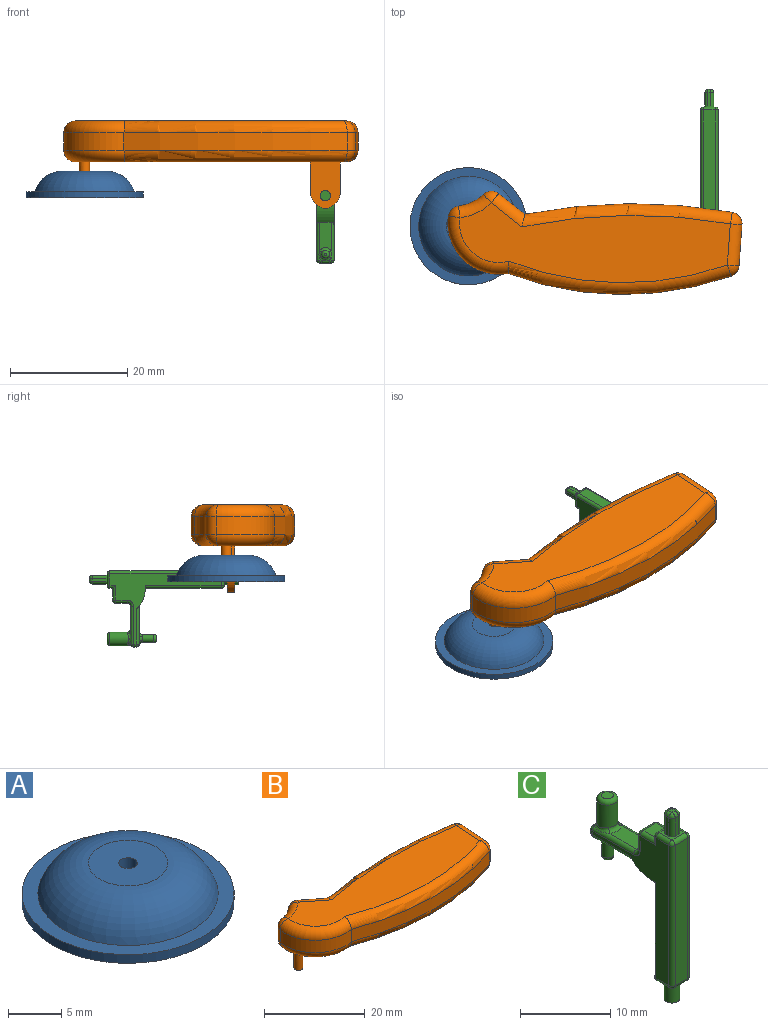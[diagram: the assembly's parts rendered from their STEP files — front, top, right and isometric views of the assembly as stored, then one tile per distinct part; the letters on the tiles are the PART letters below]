
ASSEMBLY  parts=3 mates=2
PART A: 8 faces, bbox 20x20x5 mm
  f0: cylinder r=10mm len=20mm, axis (0,0,-1), area 62.8mm2, adj f1,f2
  f1: plane 20x20mm, normal (0,0,1), area 87.2mm2, adj f0,f4
  f2: plane 20x20mm, normal (0,0,-1), area 194.2mm2, adj f0,f5
  f3: plane 7.46x7.46mm, normal (0,0,1), area 41.3mm2, adj f4,f7
  f4: torus R=3.73mm, axis (0,0,-1), area 258.3mm2, adj f1,f3
  f5: torus R=3.73mm, axis (0,0,-1), area 111.7mm2, adj f2,f6
  f6: plane 7.46x7.46mm, normal (0,0,-1), area 41.3mm2, adj f5,f7
  f7: cylinder r=0.88mm len=2.5mm, axis (0,0,1), area 13.7mm2, adj f3,f6
PART B: 47 faces, bbox 50.9x22.2x15 mm
  f0: cylinder r=96.06mm len=35.42mm, axis (0,0,-1), area 106.9mm2, adj f1,f15,f21,f24
  f1: plane 4.48x3.53mm, normal (0.62,0.78,0), area 17.1mm2, adj f0,f25,f28,f31
  f2: cylinder r=7.26mm len=4.21mm, axis (0,0,-1), area 14.2mm2, adj f18,f26,f27,f31
  f3: cylinder r=8.71mm len=10.27mm, axis (0,0,-1), area 49.4mm2, adj f4,f17,f18,f19
  f4: cylinder r=55.62mm len=38.1mm, axis (0,0,-1), area 116.7mm2, adj f3,f8,f12,f13
  f5: plane 7.03x3mm, normal (1,-0.07,0), area 21.1mm2, adj f8,f11,f14,f15
  f6: plane 46.22x13.65mm, normal (0,0,1), area 431.2mm2, adj f11,f12,f17,f21,f25,f26
  f7: plane 46.22x13.65mm, normal (0,0,-1), area 155mm2, adj f13,f14,f19,f24,f27,f28,f32,f33
  f8: cylinder r=2mm len=3mm, axis (0,0,-1), area 7mm2, adj f4,f5,f9,f10
  f9: sphere r=2mm, area 4.6mm2, adj f8,f11,f12
  f10: sphere r=2mm, area 4.6mm2, adj f8,f13,f14
  f11: cylinder r=2mm len=7.17mm, axis (-0.07,-1,0), area 22.1mm2, adj f5,f6,f9,f16
  f12: torus R=53.62mm, axis (0,0,1), area 121.2mm2, adj f4,f6,f9,f17
  f13: torus R=53.62mm, axis (0,0,1), area 121.2mm2, adj f4,f7,f10,f19
  f14: cylinder r=2mm len=7.17mm, axis (0.07,1,0), area 22.1mm2, adj f5,f7,f10,f20
  f15: cylinder r=2mm len=3mm, axis (0,0,-1), area 8.8mm2, adj f0,f5,f16,f20
  f16: sphere r=2mm, area 5.9mm2, adj f11,f15,f21
  f17: torus R=6.71mm, axis (0,0,1), area 48.1mm2, adj f3,f6,f12,f22
  f18: cylinder r=2mm len=3mm, axis (0,0,1), area 7.9mm2, adj f2,f3,f22,f23
  f19: torus R=6.71mm, axis (0,0,1), area 48.1mm2, adj f3,f7,f13,f23
  f20: sphere r=2mm, area 5.9mm2, adj f14,f15,f24
  f21: torus R=94.06mm, axis (0,0,1), area 112.1mm2, adj f0,f6,f16,f25
  f22: sphere r=2mm, area 5.3mm2, adj f17,f18,f26
  f23: sphere r=2mm, area 5.3mm2, adj f18,f19,f27
  f24: torus R=94.06mm, axis (0,0,1), area 112.1mm2, adj f0,f7,f20,f28
  f25: cylinder r=2mm len=6.44mm, axis (0.78,-0.62,0), area 19mm2, adj f1,f6,f21,f29
  f26: torus R=9.26mm, axis (0,0,1), area 16.4mm2, adj f2,f6,f22,f29
  f27: torus R=9.26mm, axis (0,0,1), area 16.4mm2, adj f2,f7,f23,f30
  f28: cylinder r=2mm len=6.44mm, axis (-0.78,0.62,0), area 19mm2, adj f1,f7,f24,f30
  f29: sphere r=2mm, area 5.8mm2, adj f25,f26,f31
  f30: sphere r=2mm, area 5.8mm2, adj f27,f28,f31
  f31: cylinder r=2mm len=3mm, axis (0,0,-1), area 8.6mm2, adj f1,f2,f29,f30
  f32: cylinder r=8.82mm len=7.3mm, axis (0,0,-1), area 24.1mm2, adj f7,f33,f36,f37
  f33: cylinder r=34.45mm len=30.65mm, axis (0,0,-1), area 95.5mm2, adj f7,f32,f34,f37
  f34: cylinder r=0.98mm len=3mm, axis (0,0,-1), area 6.5mm2, adj f7,f33,f35,f37
  f35: cylinder r=40.15mm len=36.75mm, axis (0,0,-1), area 114.7mm2, adj f7,f34,f36,f37
  f36: cylinder r=2.07mm len=4.13mm, axis (0,0,-1), area 23.4mm2, adj f7,f32,f35,f37
  f37: plane 40.56x9.64mm, normal (0,0,-1), area 267.3mm2, adj f32,f33,f34,f35,f36
  f38: cylinder r=0.88mm len=5mm, axis (0,0,1), area 27.5mm2, adj f7,f39
  f39: plane 1.75x1.75mm, normal (0,0,-1), area 2.4mm2, adj f38
  f40: plane 5x1.27mm, normal (-1,0,0), area 6.3mm2, adj f7,f41,f43,f44
  f41: plane 7.97x5.13mm, normal (0,1,0), area 34.8mm2, adj f7,f40,f42,f44,f45,f46
  f42: plane 5x1.27mm, normal (1,0,0), area 6.3mm2, adj f7,f41,f43,f45
  f43: plane 7.97x5.13mm, normal (0,-1,0), area 34.8mm2, adj f7,f40,f42,f44,f45,f46
  f44: cylinder r=3mm len=2.97mm, axis (0,-1,0), area 5.4mm2, adj f40,f41,f43,f45
  f45: cylinder r=3mm len=2.97mm, axis (0,1,0), area 5.4mm2, adj f41,f42,f43,f44
  f46: cylinder r=0.88mm len=1.75mm, axis (0,-1,0), area 7mm2, adj f41,f43
PART C: 97 faces, bbox 3x13.2x25.5 mm
  f0: plane 0.33x0.3mm, normal (0,0,-1), area 0mm2, adj f72,f79,f93
  f1: plane 0.33x0.3mm, normal (0,0,-1), area 0mm2, adj f67,f79,f91
  f2: plane 2x2mm, normal (0,0,1), area 2mm2, adj f16,f17,f18,f19,f34,f35,f38,f39
  f3: plane 12.96x2mm, normal (0,1,0), area 25.9mm2, adj f12,f21,f23,f24
  f4: plane 19x12mm, normal (-1,0,0), area 55.4mm2, adj f12,f13,f21,f25,f30,f35,f40,f42
  f5: plane 19x2mm, normal (0,-1,0), area 38mm2, adj f29,f30,f33,f34
  f6: plane 19x12mm, normal (1,0,0), area 55.4mm2, adj f12,f13,f23,f28,f33,f38,f43,f45
  f7: plane 2x0.46mm, normal (0,1,0), area 0.9mm2, adj f14,f39,f40,f43
  f8: plane 2x2mm, normal (0,0,-1), area 1.6mm2, adj f24,f25,f28,f29,f95
  f9: plane 4.28x2mm, normal (0,0,1), area 8.1mm2, adj f48,f52,f54,f86
  f10: plane 4.94x2mm, normal (0,0,-1), area 9.1mm2, adj f13,f67,f72,f80
  f11: plane 2x0.53mm, normal (0,1,0), area 1mm2, adj f68,f70,f73,f91,f92,f93
  f12: plane 3x0.51mm, normal (0,0,-1), area 0.1mm2, adj f3,f4,f6,f13,f21,f23
  f13: cylinder r=4.8mm len=3.53mm, axis (-1,0,0), area 9.8mm2, adj f4,f6,f10,f12,f67,f72
  f14: plane 2x2mm, normal (0,0,1), area 4mm2, adj f7,f42,f45,f46
  f15: plane 2.05x2mm, normal (0,1,0), area 4.1mm2, adj f46,f47,f51,f52
  f16: plane 2.5x0.5mm, normal (-1,0,0), area 1.2mm2, adj f2,f57,f63,f66
  f17: plane 2.5x0.5mm, normal (0,-1,0), area 1.2mm2, adj f2,f60,f64,f66
  f18: plane 2.5x0.5mm, normal (1,0,0), area 1.2mm2, adj f2,f55,f59,f60
  f19: plane 2.5x0.5mm, normal (0,1,0), area 1.2mm2, adj f2,f55,f57,f58
  f20: plane 0.5x0.5mm, normal (0,0,1), area 0.3mm2, adj f58,f59,f63,f64
  f21: cylinder r=0.5mm len=12.96mm, axis (0,0,-1), area 10.2mm2, adj f3,f4,f12,f22
  f22: sphere r=0.5mm, area 0.4mm2, adj f21,f24,f25
  f23: cylinder r=0.5mm len=12.96mm, axis (0,0,1), area 10.2mm2, adj f3,f6,f12,f26
  f24: cylinder r=0.5mm len=2mm, axis (-1,0,0), area 1.6mm2, adj f3,f8,f22,f26
  f25: cylinder r=0.5mm len=2mm, axis (0,-1,0), area 1.6mm2, adj f4,f8,f22,f27
  f26: sphere r=0.5mm, area 0.4mm2, adj f23,f24,f28
  f27: sphere r=0.5mm, area 0.4mm2, adj f25,f29,f30
  f28: cylinder r=0.5mm len=2mm, axis (0,1,0), area 1.6mm2, adj f6,f8,f26,f31
  f29: cylinder r=0.5mm len=2mm, axis (1,0,0), area 1.6mm2, adj f5,f8,f27,f31
  f30: cylinder r=0.5mm len=19mm, axis (0,0,1), area 14.9mm2, adj f4,f5,f27,f32
  f31: sphere r=0.5mm, area 0.4mm2, adj f28,f29,f33
  f32: sphere r=0.5mm, area 0.4mm2, adj f30,f34,f35
  f33: cylinder r=0.5mm len=19mm, axis (0,0,-1), area 14.9mm2, adj f5,f6,f31,f36
  f34: cylinder r=0.5mm len=2mm, axis (-1,0,0), area 1.6mm2, adj f2,f5,f32,f36
  f35: cylinder r=0.5mm len=2mm, axis (0,1,0), area 1.6mm2, adj f2,f4,f32,f37
  f36: sphere r=0.5mm, area 0.4mm2, adj f33,f34,f38
  f37: sphere r=0.5mm, area 0.4mm2, adj f35,f39,f40
  f38: cylinder r=0.5mm len=2mm, axis (0,-1,0), area 1.6mm2, adj f2,f6,f36,f41
  f39: cylinder r=0.5mm len=2mm, axis (1,0,0), area 1.6mm2, adj f2,f7,f37,f41
  f40: cylinder r=0.5mm len=0.96mm, axis (0,0,-1), area 0.5mm2, adj f4,f7,f37,f42
  f41: sphere r=0.5mm, area 0.4mm2, adj f38,f39,f43
  f42: cylinder r=0.5mm len=2.5mm, axis (0,1,0), area 1.7mm2, adj f4,f14,f40,f44
  f43: cylinder r=0.5mm len=0.96mm, axis (0,0,1), area 0.5mm2, adj f6,f7,f41,f45
  f44: sphere r=0.5mm, area 0.4mm2, adj f42,f46,f47
  f45: cylinder r=0.5mm len=2.5mm, axis (0,-1,0), area 1.7mm2, adj f6,f14,f43,f49
  f46: cylinder r=0.5mm len=2mm, axis (-1,0,0), area 1.6mm2, adj f14,f15,f44,f49
  f47: cylinder r=0.5mm len=2.05mm, axis (0,0,-1), area 1.6mm2, adj f4,f15,f44,f50
  f48: cylinder r=0.5mm len=6.5mm, axis (0,1,0), area 4.5mm2, adj f4,f9,f50,f71,f84
  f49: sphere r=0.5mm, area 0.4mm2, adj f45,f46,f51
  f50: torus R=1mm, axis (-1,0,0), area 0.8mm2, adj f4,f47,f48,f52
  f51: cylinder r=0.5mm len=2.05mm, axis (0,0,1), area 1.6mm2, adj f6,f15,f49,f53
  f52: cylinder r=0.5mm len=2mm, axis (1,0,0), area 1.6mm2, adj f9,f15,f50,f53
  f53: torus R=1mm, axis (-1,0,0), area 0.8mm2, adj f6,f51,f52,f54
  f54: cylinder r=0.5mm len=6.5mm, axis (0,-1,0), area 4.5mm2, adj f6,f9,f53,f69,f88
  f55: cylinder r=0.5mm len=2.5mm, axis (0,0,1), area 2mm2, adj f2,f18,f19,f56
  f56: sphere r=0.5mm, area 0.4mm2, adj f55,f58,f59
  f57: cylinder r=0.5mm len=2.5mm, axis (0,0,-1), area 2mm2, adj f2,f16,f19,f61
  f58: cylinder r=0.5mm len=0.5mm, axis (1,0,0), area 0.4mm2, adj f19,f20,f56,f61
  f59: cylinder r=0.5mm len=0.5mm, axis (0,-1,0), area 0.4mm2, adj f18,f20,f56,f62
  f60: cylinder r=0.5mm len=2.5mm, axis (0,0,-1), area 2mm2, adj f2,f17,f18,f62
  f61: sphere r=0.5mm, area 0.4mm2, adj f57,f58,f63
  f62: sphere r=0.5mm, area 0.4mm2, adj f59,f60,f64
  f63: cylinder r=0.5mm len=0.5mm, axis (0,1,0), area 0.4mm2, adj f16,f20,f61,f65
  f64: cylinder r=0.5mm len=0.5mm, axis (-1,0,0), area 0.4mm2, adj f17,f20,f62,f65
  f65: sphere r=0.5mm, area 0.4mm2, adj f63,f64,f66
  f66: cylinder r=0.5mm len=2.5mm, axis (0,0,1), area 2mm2, adj f2,f16,f17,f65
  f67: cylinder r=0.5mm len=6.5mm, axis (0,1,0), area 4.8mm2, adj f1,f6,f10,f13,f81,f90
  f68: cylinder r=0.5mm len=0.5mm, axis (0,0,1), area 0.4mm2, adj f6,f11,f69,f90
  f69: sphere r=0.5mm, area 0.4mm2, adj f54,f68,f70,f87
  f70: cylinder r=0.5mm len=2mm, axis (-1,0,0), area 0.8mm2, adj f11,f69,f71,f85
  f71: sphere r=0.5mm, area 0.4mm2, adj f48,f70,f73,f83
  f72: cylinder r=0.5mm len=6.5mm, axis (0,-1,0), area 4.8mm2, adj f0,f4,f10,f13,f78,f94
  f73: cylinder r=0.5mm len=0.5mm, axis (0,0,-1), area 0.4mm2, adj f4,f11,f71,f94
  f74: cylinder r=1.17mm len=3.39mm, axis (0,0,-1), area 23.2mm2, adj f83,f84,f85,f86,f87,f88,f89
  f75: plane 1.35x1.35mm, normal (0,0,1), area 1.4mm2, adj f89
  f76: cylinder r=0.68mm len=2mm, axis (0,0,1), area 8.5mm2, adj f78,f79,f80,f81,f82
  f77: plane 0.35x0.35mm, normal (0,0,-1), area 0.1mm2, adj f82
  f78: bspline ~1.46x0.59mm, area 0.7mm2, adj f72,f76,f79,f80
  f79: torus R=1.18mm, axis (0,0,-1), area 1.3mm2, adj f0,f1,f76,f78,f81,f92
  f80: torus R=1.18mm, axis (0,0,-1), area 1.4mm2, adj f10,f76,f78,f81
  f81: bspline ~1.46x0.59mm, area 0.7mm2, adj f67,f76,f79,f80
  f82: torus R=0.18mm, axis (0,0,-1), area 2.4mm2, adj f76,f77
  f83: bspline ~0.65x0.58mm, area 0.2mm2, adj f71,f74,f84,f85
  f84: bspline ~2.6x0.77mm, area 1mm2, adj f48,f74,f83,f86
  f85: bspline ~2.41x0.66mm, area 0.8mm2, adj f70,f74,f83,f87
  f86: torus R=1.67mm, axis (0,0,-1), area 1.4mm2, adj f9,f74,f84,f88
  f87: bspline ~0.64x0.59mm, area 0.2mm2, adj f69,f74,f85,f88
  f88: bspline ~2.6x0.77mm, area 1mm2, adj f54,f74,f86,f87
  f89: torus R=0.67mm, axis (0,0,1), area 4.9mm2, adj f74,f75
  f90: sphere r=0.5mm, area 0.4mm2, adj f67,f68,f91
  f91: cylinder r=0.5mm len=0.5mm, axis (1,0,0), area 0.2mm2, adj f1,f11,f90,f92
  f92: bspline ~1.91x0.62mm, area 1mm2, adj f11,f79,f91,f93
  f93: cylinder r=0.5mm len=0.5mm, axis (1,0,0), area 0.2mm2, adj f0,f11,f92,f94
  f94: sphere r=0.5mm, area 0.4mm2, adj f72,f73,f93
  f95: cylinder r=0.88mm len=2.5mm, axis (0,0,1), area 13.7mm2, adj f8,f96
  f96: plane 1.75x1.75mm, normal (0,0,-1), area 2.4mm2, adj f95
PLACE A rot(axis=(0,0,1),0deg) t=(-53.63,2.22,26.51)mm
PLACE B rot(axis=(0,0,1),0deg) t=(-23.47,-15.42,32.58)mm
PLACE C rot(axis=(-1,0,0),90deg) t=(-12.52,2.56,26.83)mm
MATE cylindrical C.f95 <-> B.f46  axis (0,1,0) through (-12.52,0.06,26.83)mm
MATE cylindrical A.f7 <-> B.f38  axis (0,0,1) through (-53.63,2.22,31.01)mm
